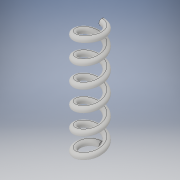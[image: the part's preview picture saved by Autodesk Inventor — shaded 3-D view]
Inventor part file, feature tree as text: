
AUTODESK INVENTOR PART (.ipt)
format: ipt  version: 2019 (Build 230136000, 136)  size: 437,248 bytes
history: native  units: in
note: dims shown in document units (in); Inventor stores cm internally (conversion verified against a paired STEP export)
features: helix x1, sketch x1
ambient origin geometry x8: Origin, YZ Plane, XZ Plane, XY Plane, X Axis, Y Axis, Z Axis, Center Point
bodies: Solid1 (feature_tree)
feature tree (2):
  helix  "Coil1"  [1 undecoded]
  sketch  "Sketch1"  dims[d1=0.0984in d2=1.7717in d3=0.3937in d4=1.7717in d5=1.9685in d6=0.0in d7=90.0deg d8=90.0deg d9=90.0deg d10=90.0deg]
note: 1 required parameter value undecoded (feature->parameter linkage not recoverable at this tier; creation-order binding heuristic only, values carry confidence <= 0.55)
